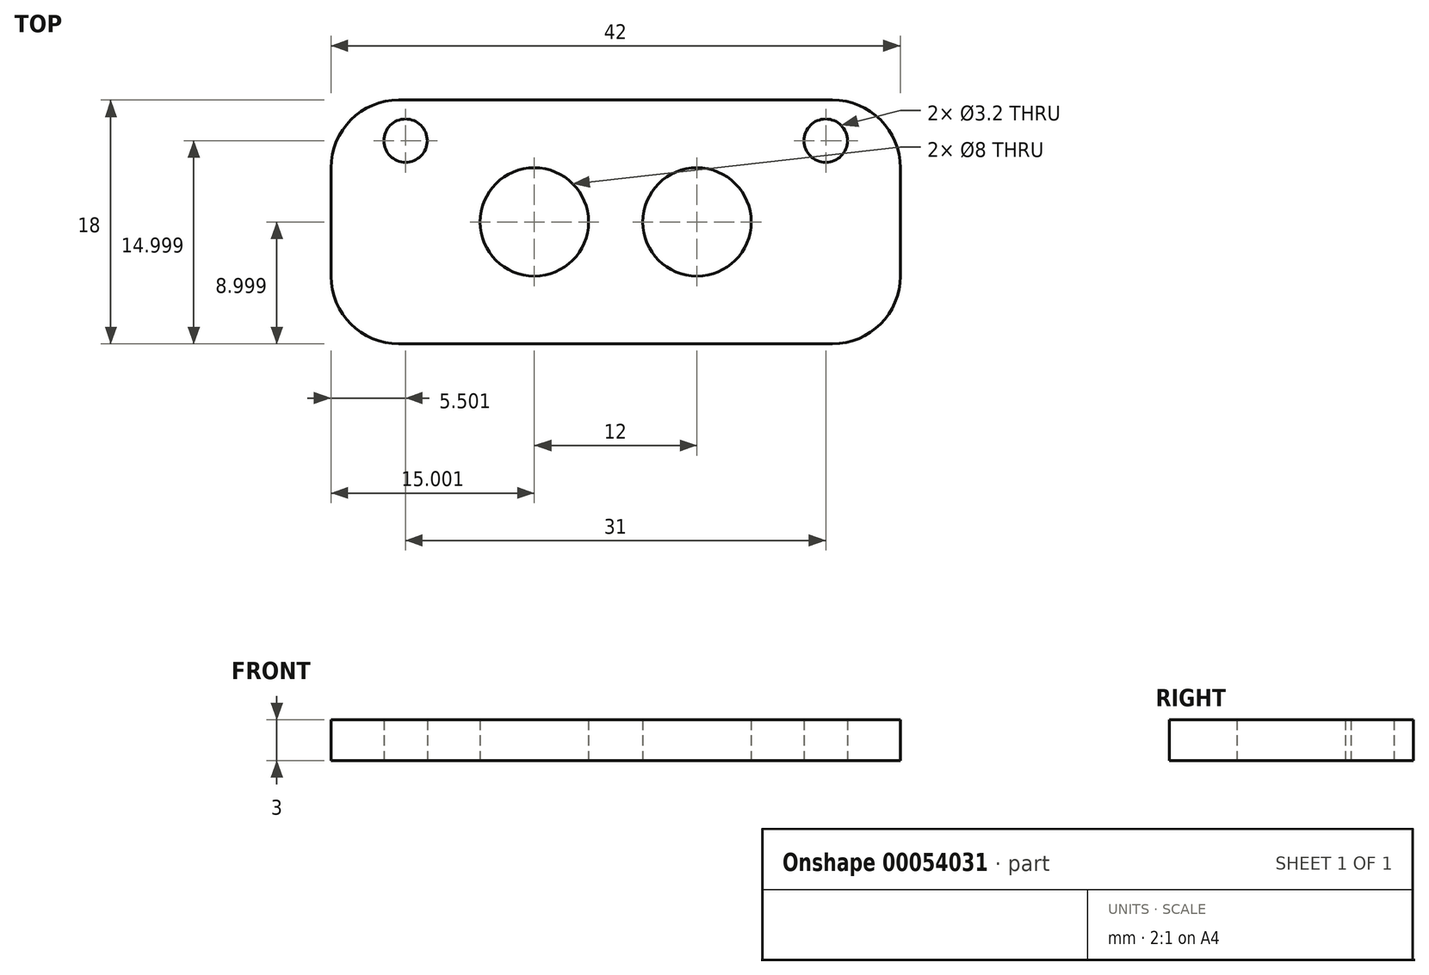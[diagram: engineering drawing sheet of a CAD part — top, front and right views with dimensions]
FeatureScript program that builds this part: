
annotation { "Feature Type Name" : "Feature", "Feature Type Description" : "" }
export const myFeature = defineFeature(function(context is Context, id is Id, definition is map)
    precondition{}
    {
        {
            var Q0;
            Q0=qCreatedBy(makeId("Top.planeOp"),FACE);
            var sketch = newSketch(context, id + "F0", { "sketchPlane" : qUnion([Q0])});
            skLineSegment(sketch, "E0.bottom", {"start": v(-52.32, 28.22) * mm, "end": v(-10.32, 28.22) * mm});
            skLineSegment(sketch, "E0.top", {"start": v(-52.32, 10.22) * mm, "end": v(-10.32, 10.22) * mm});
            skLineSegment(sketch, "E0.left", {"start": v(-52.32, 28.22) * mm, "end": v(-52.32, 10.22) * mm});
            skLineSegment(sketch, "E0.right", {"start": v(-10.32, 28.22) * mm, "end": v(-10.32, 10.22) * mm});
            skPoint(sketch, "E1", {"position": v(-46.82, 25.22) * mm});
            skPoint(sketch, "E2", {"position": v(-15.82, 25.22) * mm});
            skPoint(sketch, "E3", {"position": v(-25.32, 19.22) * mm});
            skPoint(sketch, "E4", {"position": v(-37.32, 19.22) * mm});
            skSolve(sketch);
        }
        {
            var Q0;
            Q0 = qSketchRegion(id + "F0", true);
            extrude(context, id + "F1", {"entities" : qUnion([Q0]), "depth" : 3 * mm});
        }
        {
            var Q0;
            Q0=sQuery(id+"F0.wireOp",VERTEX,"E1");
            var Q1;
            Q1=sQuery(id+"F0.wireOp",VERTEX,"E2");
            var Q2;
            Q2=makeQuery(id+"F1.opExtrude","SWEPT_BODY",BODY,{"disambiguationData":[OSD([sQuery(id+"F0.wireOp",EDGE,"E0.bottom"),sQuery(id+"F0.wireOp",EDGE,"E0.top"),sQuery(id+"F0.wireOp",EDGE,"E0.left"),sQuery(id+"F0.wireOp",EDGE,"E0.right")])]});
            hole(context, id + "F2", {"style" : HoleStyle.SIMPLE, "holeDiameter" : 3.2 * mm, "endStyle" : HoleEndStyle.THROUGH, "oppositeDirection" : true, "locations" : qUnion([Q0, Q1]), "scope" : qUnion([Q2])});
        }
        {
            var Q0;
            Q0=sQuery(id+"F0.wireOp",VERTEX,"E3");
            var Q1;
            Q1=sQuery(id+"F0.wireOp",VERTEX,"E4");
            var Q2;
            Q2=makeQuery(id+"F1.opExtrude","SWEPT_BODY",BODY,{"disambiguationData":[OSD([sQuery(id+"F0.wireOp",EDGE,"E0.bottom"),sQuery(id+"F0.wireOp",EDGE,"E0.top"),sQuery(id+"F0.wireOp",EDGE,"E0.left"),sQuery(id+"F0.wireOp",EDGE,"E0.right")])]});
            hole(context, id + "F3", {"style" : HoleStyle.SIMPLE, "holeDiameter" : 8 * mm, "endStyle" : HoleEndStyle.THROUGH, "oppositeDirection" : true, "locations" : qUnion([Q0, Q1]), "scope" : qUnion([Q2])});
        }
        {
            var Q0;
            Q0=makeQuery(id+"F1.opExtrude","SWEPT_EDGE",EDGE,{"disambiguationData":[OSD([sQuery(id+"F0.wireOp",EDGE,"E0.bottom"),sQuery(id+"F0.wireOp",EDGE,"E0.left")])]});
            var Q1;
            Q1=makeQuery(id+"F1.opExtrude","SWEPT_EDGE",EDGE,{"disambiguationData":[OSD([sQuery(id+"F0.wireOp",EDGE,"E0.top"),sQuery(id+"F0.wireOp",EDGE,"E0.left")])]});
            var Q2;
            Q2=makeQuery(id+"F1.opExtrude","SWEPT_EDGE",EDGE,{"disambiguationData":[OSD([sQuery(id+"F0.wireOp",EDGE,"E0.bottom"),sQuery(id+"F0.wireOp",EDGE,"E0.right")])]});
            var Q3;
            Q3=makeQuery(id+"F1.opExtrude","SWEPT_EDGE",EDGE,{"disambiguationData":[OSD([sQuery(id+"F0.wireOp",EDGE,"E0.top"),sQuery(id+"F0.wireOp",EDGE,"E0.right")])]});
            fillet(context, id + "F4", {"entities" : qUnion([Q0, Q1, Q2, Q3]), "radius" : 5 * mm, "tangentPropagation" : true, "allowEdgeOverflow" : false});
        }
    });
